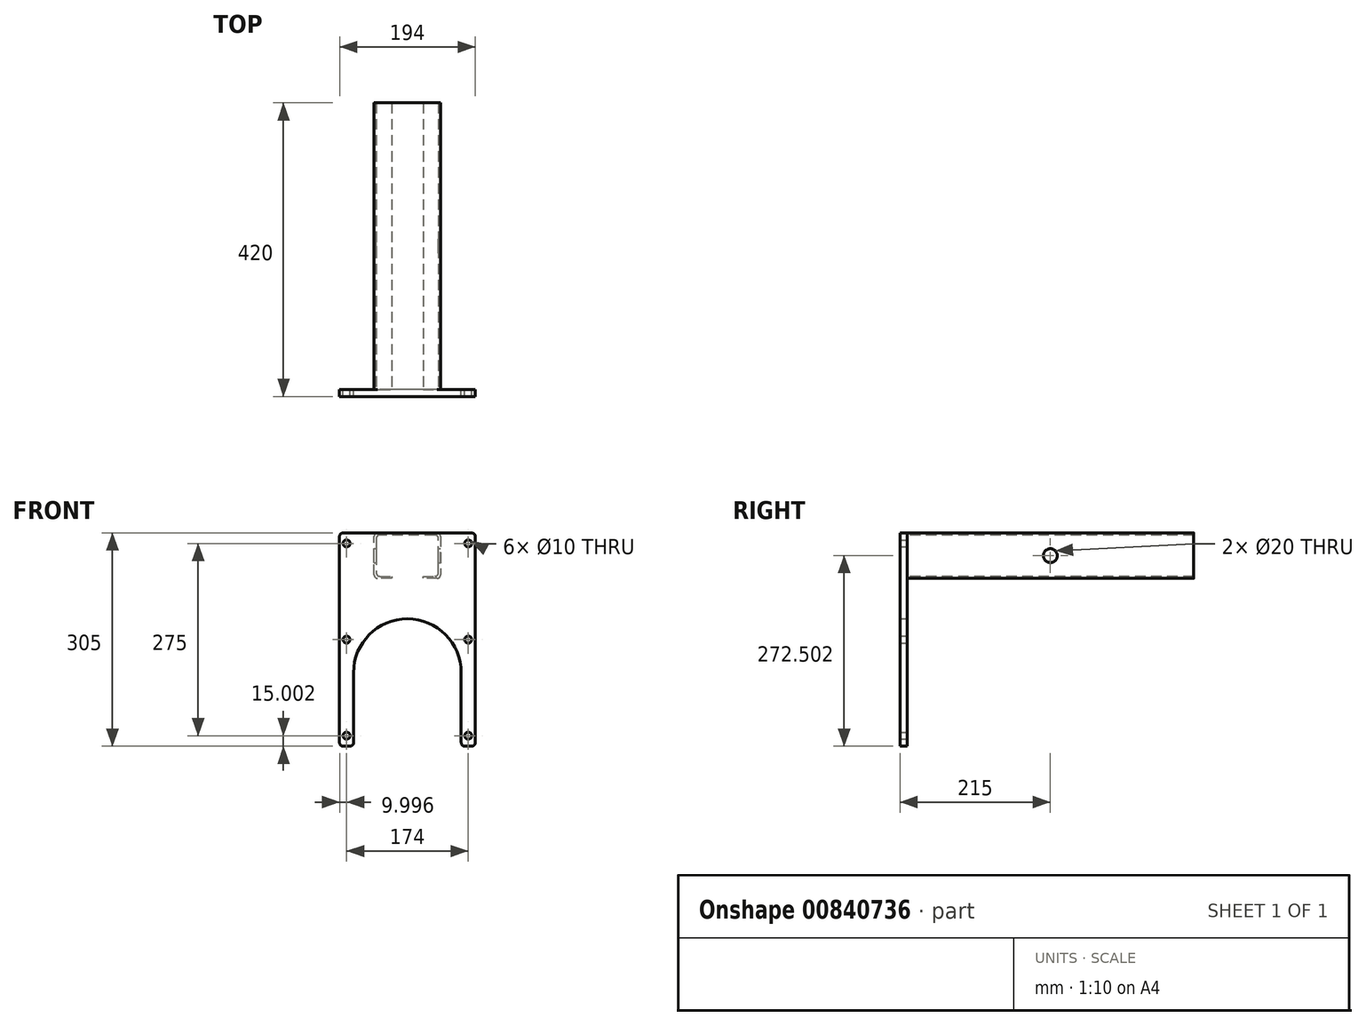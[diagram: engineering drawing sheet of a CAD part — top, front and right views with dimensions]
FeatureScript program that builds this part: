
annotation { "Feature Type Name" : "Feature", "Feature Type Description" : "" }
export const myFeature = defineFeature(function(context is Context, id is Id, definition is map)
    precondition{}
    {
        {
            var Q0;
            Q0=qCreatedBy(makeId("Front.planeOp"),FACE);
            var sketch = newSketch(context, id + "F0", { "sketchPlane" : qUnion([Q0])});
            skLineSegment(sketch, "E0", {"start": v(-79.8, -17.1) * mm, "end": v(-79.8, -122.2) * mm});
            skLineSegment(sketch, "E1", {"start": v(-79.8, -122.2) * mm, "end": v(-99.8, -122.2) * mm});
            skLineSegment(sketch, "E2", {"start": v(-99.8, -122.2) * mm, "end": v(-99.8, 182.8) * mm});
            skLineSegment(sketch, "E3", {"start": v(-99.8, 182.8) * mm, "end": v(94.2, 182.8) * mm});
            skLineSegment(sketch, "E4", {"start": v(94.2, 182.8) * mm, "end": v(94.2, -122.2) * mm});
            skLineSegment(sketch, "E5", {"start": v(94.2, -122.2) * mm, "end": v(74.2, -122.2) * mm});
            skLineSegment(sketch, "E6", {"start": v(74.2, -122.2) * mm, "end": v(74.2, -17.1) * mm});
            skArc(sketch, "E7", {"start": v(-79.8, -17.1) * mm, "mid": v(-2.8, 59.9) * mm, "end": v(74.2, -17.1) * mm});
            skSolve(sketch);
        }
        {
            var Q0;
            Q0 = qSketchRegion(id + "F0", true);
            extrude(context, id + "F1", {"entities" : qUnion([Q0]), "depth" : 10 * mm, "offsetDistance" : 25 * mm});
        }
        {
            var Q0;
            Q0=makeQuery(id+"F1.opExtrude","CAP_FACE",FACE,{"disambiguationData":[OSD([sQuery(id+"F0.wireOp",EDGE,"E0"),sQuery(id+"F0.wireOp",EDGE,"E1"),sQuery(id+"F0.wireOp",EDGE,"E2"),sQuery(id+"F0.wireOp",EDGE,"E3"),sQuery(id+"F0.wireOp",EDGE,"E4"),sQuery(id+"F0.wireOp",EDGE,"E5"),sQuery(id+"F0.wireOp",EDGE,"E6"),sQuery(id+"F0.wireOp",EDGE,"E7")])],"isStart":true});
            var sketch = newSketch(context, id + "F2", { "sketchPlane" : qUnion([Q0])});
            skLineSegment(sketch, "E8", {"start": v(50.3, 182.8) * mm, "end": v(-44.7, 182.8) * mm});
            skLineSegment(sketch, "E9", {"start": v(-44.7, 182.8) * mm, "end": v(-44.7, 117.8) * mm});
            skLineSegment(sketch, "E10", {"start": v(-44.7, 117.8) * mm, "end": v(-19.7, 117.8) * mm});
            skLineSegment(sketch, "E11", {"start": v(-19.7, 117.8) * mm, "end": v(-19.7, 120.8) * mm});
            skLineSegment(sketch, "E12", {"start": v(-19.7, 120.8) * mm, "end": v(-41.7, 120.8) * mm});
            skLineSegment(sketch, "E13", {"start": v(-41.7, 120.8) * mm, "end": v(-41.7, 179.8) * mm});
            skLineSegment(sketch, "E14", {"start": v(-41.7, 179.8) * mm, "end": v(47.3, 179.8) * mm});
            skLineSegment(sketch, "E15", {"start": v(47.3, 179.8) * mm, "end": v(47.3, 120.8) * mm});
            skLineSegment(sketch, "E16", {"start": v(47.3, 120.8) * mm, "end": v(25.3, 120.8) * mm});
            skLineSegment(sketch, "E17", {"start": v(25.3, 120.8) * mm, "end": v(25.3, 117.8) * mm});
            skLineSegment(sketch, "E18", {"start": v(25.3, 117.8) * mm, "end": v(50.3, 117.8) * mm});
            skLineSegment(sketch, "E19", {"start": v(50.3, 117.8) * mm, "end": v(50.3, 182.8) * mm});
            skSolve(sketch);
        }
        {
            var Q0;
            Q0 = qSketchRegion(id + "F2", true);
            extrude(context, id + "F3", {"entities" : qUnion([Q0]), "operationType" : NewBodyOperationType.ADD, "depth" : 410 * mm, "offsetDistance" : 25 * mm});
        }
        {
            var Q0;
            Q0=makeQuery(id+"F3.opExtrude","SWEPT_EDGE",EDGE,{"disambiguationData":[OSD([sQuery(id+"F0.wireOp",EDGE,"E3"),sQuery(id+"F2.wireOp",EDGE,"E8"),sQuery(id+"F2.wireOp",EDGE,"E9")])]});
            var Q1;
            Q1=makeQuery(id+"F3.opExtrude","SWEPT_EDGE",EDGE,{"disambiguationData":[OSD([sQuery(id+"F0.wireOp",EDGE,"E3"),sQuery(id+"F2.wireOp",EDGE,"E8"),sQuery(id+"F2.wireOp",EDGE,"E19")])]});
            var Q2;
            Q2=makeQuery(id+"F3.opExtrude","SWEPT_EDGE",EDGE,{"disambiguationData":[OSD([sQuery(id+"F2.wireOp",EDGE,"E18"),sQuery(id+"F2.wireOp",EDGE,"E19")])]});
            var Q3;
            Q3=makeQuery(id+"F3.opExtrude","SWEPT_EDGE",EDGE,{"disambiguationData":[OSD([sQuery(id+"F2.wireOp",EDGE,"E9"),sQuery(id+"F2.wireOp",EDGE,"E10")])]});
            var Q4;
            Q4=makeQuery(id+"F3.opExtrude","SWEPT_EDGE",EDGE,{"disambiguationData":[OSD([sQuery(id+"F2.wireOp",EDGE,"E14"),sQuery(id+"F2.wireOp",EDGE,"E15")])]});
            var Q5;
            Q5=makeQuery(id+"F3.opExtrude","SWEPT_EDGE",EDGE,{"disambiguationData":[OSD([sQuery(id+"F2.wireOp",EDGE,"E15"),sQuery(id+"F2.wireOp",EDGE,"E16")])]});
            var Q6;
            Q6=makeQuery(id+"F3.opExtrude","SWEPT_EDGE",EDGE,{"disambiguationData":[OSD([sQuery(id+"F2.wireOp",EDGE,"E12"),sQuery(id+"F2.wireOp",EDGE,"E13")])]});
            var Q7;
            Q7=makeQuery(id+"F3.opExtrude","SWEPT_EDGE",EDGE,{"disambiguationData":[OSD([sQuery(id+"F2.wireOp",EDGE,"E13"),sQuery(id+"F2.wireOp",EDGE,"E14")])]});
            fillet(context, id + "F4", {"entities" : qUnion([Q0, Q1, Q2, Q3, Q4, Q5, Q6, Q7]), "radius" : 5 * mm, "tangentPropagation" : true, "allowEdgeOverflow" : false});
        }
        {
            var Q0;
            Q0=makeQuery(id+"F1.opExtrude","SWEPT_EDGE",EDGE,{"disambiguationData":[OSD([sQuery(id+"F0.wireOp",EDGE,"E1"),sQuery(id+"F0.wireOp",EDGE,"E2")])]});
            var Q1;
            Q1=makeQuery(id+"F1.opExtrude","SWEPT_EDGE",EDGE,{"disambiguationData":[OSD([sQuery(id+"F0.wireOp",EDGE,"E2"),sQuery(id+"F0.wireOp",EDGE,"E3")])]});
            var Q2;
            Q2=makeQuery(id+"F1.opExtrude","SWEPT_EDGE",EDGE,{"disambiguationData":[OSD([sQuery(id+"F0.wireOp",EDGE,"E3"),sQuery(id+"F0.wireOp",EDGE,"E4")])]});
            var Q3;
            Q3=makeQuery(id+"F1.opExtrude","SWEPT_EDGE",EDGE,{"disambiguationData":[OSD([sQuery(id+"F0.wireOp",EDGE,"E4"),sQuery(id+"F0.wireOp",EDGE,"E5")])]});
            var Q4;
            Q4=makeQuery(id+"F1.opExtrude","SWEPT_EDGE",EDGE,{"disambiguationData":[OSD([sQuery(id+"F0.wireOp",EDGE,"E5"),sQuery(id+"F0.wireOp",EDGE,"E6")])]});
            var Q5;
            Q5=makeQuery(id+"F1.opExtrude","SWEPT_EDGE",EDGE,{"disambiguationData":[OSD([sQuery(id+"F0.wireOp",EDGE,"E0"),sQuery(id+"F0.wireOp",EDGE,"E1")])]});
            fillet(context, id + "F5", {"entities" : qUnion([Q0, Q1, Q2, Q3, Q4, Q5]), "radius" : 5 * mm, "tangentPropagation" : true, "allowEdgeOverflow" : false});
        }
        {
            var Q0;
            Q0=makeQuery(id+"F1.opExtrude","CAP_FACE",FACE,{"disambiguationData":[OSD([sQuery(id+"F0.wireOp",EDGE,"E0"),sQuery(id+"F0.wireOp",EDGE,"E1"),sQuery(id+"F0.wireOp",EDGE,"E2"),sQuery(id+"F0.wireOp",EDGE,"E3"),sQuery(id+"F0.wireOp",EDGE,"E4"),sQuery(id+"F0.wireOp",EDGE,"E5"),sQuery(id+"F0.wireOp",EDGE,"E6"),sQuery(id+"F0.wireOp",EDGE,"E7")])],"isStart":true});
            var sketch = newSketch(context, id + "F6", { "sketchPlane" : qUnion([Q0])});
            skCircle(sketch, "E20", {"center": v(-84.2, 167.8) * mm, "radius": 5 * mm});
            skCircle(sketch, "E21", {"center": v(-84.2, 30.3) * mm, "radius": 5 * mm});
            skCircle(sketch, "E22", {"center": v(-84.2, -107.2) * mm, "radius": 5 * mm});
            skCircle(sketch, "E23", {"center": v(89.8, 167.8) * mm, "radius": 5 * mm});
            skCircle(sketch, "E24", {"center": v(89.8, 30.3) * mm, "radius": 5 * mm});
            skCircle(sketch, "E25", {"center": v(89.8, -107.2) * mm, "radius": 5 * mm});
            skSolve(sketch);
        }
        {
            var Q0;
            Q0 = qSketchRegion(id + "F6", true);
            extrude(context, id + "F7", {"entities" : qUnion([Q0]), "operationType" : NewBodyOperationType.REMOVE, "endBound" : BoundingType.THROUGH_ALL, "oppositeDirection" : true, "depth" : 25 * mm, "offsetDistance" : 25 * mm});
        }
        {
            var Q0;
            Q0=makeQuery(id+"F3.opExtrude","SWEPT_FACE",FACE,{"disambiguationData":[OSD([sQuery(id+"F2.wireOp",EDGE,"E9")])]});
            var sketch = newSketch(context, id + "F8", { "sketchPlane" : qUnion([Q0])});
            skCircle(sketch, "E26", {"center": v(205, 150.3) * mm, "radius": 10 * mm});
            skSolve(sketch);
        }
        {
            var Q0;
            Q0 = qSketchRegion(id + "F8", true);
            extrude(context, id + "F9", {"entities" : qUnion([Q0]), "operationType" : NewBodyOperationType.REMOVE, "endBound" : BoundingType.THROUGH_ALL, "oppositeDirection" : true, "depth" : 25 * mm, "offsetDistance" : 25 * mm});
        }
    });
